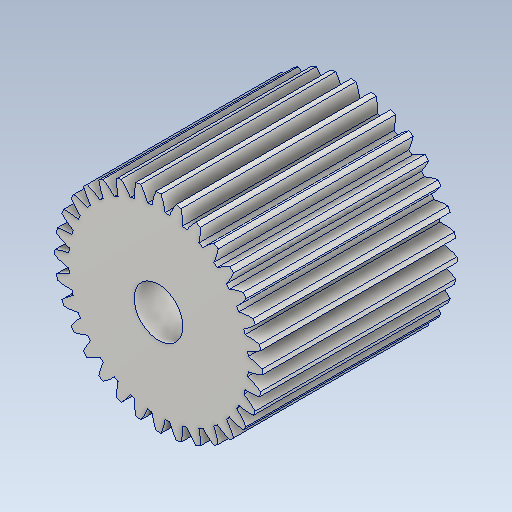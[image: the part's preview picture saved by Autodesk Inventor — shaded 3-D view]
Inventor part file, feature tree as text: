
AUTODESK INVENTOR PART (.ipt)
format: ipt  version: 2021 (Build 250183000, 183)  size: 373,248 bytes
history: native  units: mm
features: other x13, sketch x3, plane x2
ambient origin geometry x8: Origin, YZ Plane, XZ Plane, XY Plane, X Axis, Y Axis, Z Axis, Center Point
bodies: Solid1 (feature_tree)
feature tree (18):
  other  "Spur Gear1"
  other  "Solid1::Spur Gear1"
  other  "TaggingFeature1"
  sketch  "Sketch1"  dims[d0=10.0mm]
  sketch  "Sketch2"  dims[d16=80.0mm d17=0.0mm d41=0.0mm d43=80.0mm d46=80.0mm d47=0.0mm d48=0.0mm]
  sketch  "Sketch3"
  plane  "XZ Plane_1"
  plane  "Work Plane2"
  other  "Z Axis_1"
  other  "Srf1"
  other  "Srf1::Derived"
  other  "Distance iMate"
  other  "Align iMate"
  other  "Mesh iMate"
  other  "Axis iMate"
  other  "Position iMate"
  other  "Mesh iMate2"
  other  "Start plane iMate"
